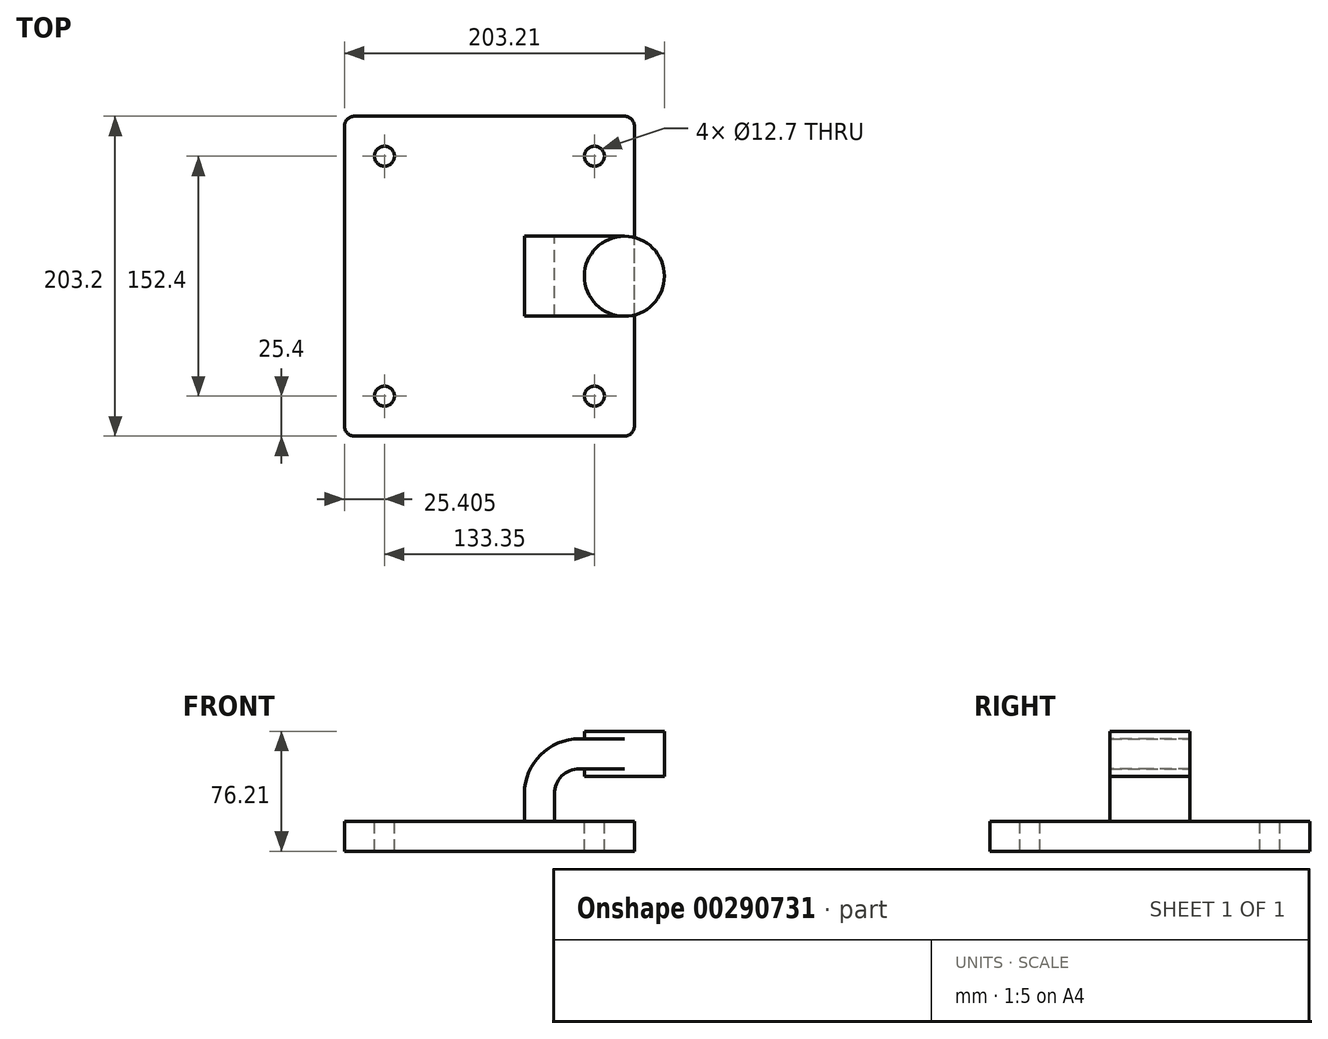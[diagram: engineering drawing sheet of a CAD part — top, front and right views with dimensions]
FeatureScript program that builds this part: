
annotation { "Feature Type Name" : "Feature", "Feature Type Description" : "" }
export const myFeature = defineFeature(function(context is Context, id is Id, definition is map)
    precondition{}
    {
        {
            var Q0;
            Q0=qCreatedBy(makeId("Front.planeOp"),FACE);
            var sketch = newSketch(context, id + "F0", { "sketchPlane" : qUnion([Q0])});
            skLineSegment(sketch, "E0.bottom", {"start": v(-41.28, -9.52) * mm, "end": v(41.28, -9.52) * mm});
            skLineSegment(sketch, "E0.top", {"start": v(-41.28, 9.53) * mm, "end": v(41.27, 9.53) * mm});
            skPoint(sketch, "E0.middle", {"position": v(0, 0) * mm});
            skLineSegment(sketch, "E1.bottom", {"start": v(60.32, 38.1) * mm, "end": v(111.12, 38.1) * mm});
            skLineSegment(sketch, "E1.top", {"start": v(60.32, 66.68) * mm, "end": v(111.12, 66.68) * mm});
            skLineSegment(sketch, "E1.left", {"start": v(60.32, 38.1) * mm, "end": v(60.32, 66.68) * mm});
            skLineSegment(sketch, "E1.right", {"start": v(111.12, 38.1) * mm, "end": v(111.12, 66.68) * mm});
            skPoint(sketch, "E1.middle", {"position": v(85.72, 52.39) * mm});
            skLineSegment(sketch, "E2", {"start": v(41.27, 9.52) * mm, "end": v(41.27, 27) * mm});
            skArc(sketch, "E3", {"start": v(41.27, 27) * mm, "mid": v(45.92, 38.23) * mm, "end": v(57.15, 42.88) * mm});
            skLineSegment(sketch, "E4", {"start": v(57.15, 42.88) * mm, "end": v(85.72, 42.88) * mm});
            skLineSegment(sketch, "E5.0", {"start": v(57.15, 61.93) * mm, "end": v(85.72, 61.93) * mm});
            skArc(sketch, "E5.1", {"start": v(22.22, 27) * mm, "mid": v(32.45, 51.7) * mm, "end": v(57.15, 61.93) * mm});
            skLineSegment(sketch, "E5.2", {"start": v(22.22, 9.52) * mm, "end": v(22.22, 27) * mm});
            skFitSpline(sketch, "E6", {"points": [v(-41.28, 9.52) * mm, v(57.15, 61.93) * mm], "startDerivative": vector(0.35, 59.87) * mm, "endDerivative": vector(73.58, -1.05) * mm});
            skLineSegment(sketch, "E7", {"start": v(85.72, 38.1) * mm, "end": v(85.72, 66.68) * mm});
            skLineSegment(sketch, "E8", {"start": v(-41.28, 9.53) * mm, "end": v(-92.08, 9.53) * mm});
            skLineSegment(sketch, "E9", {"start": v(-92.08, 9.52) * mm, "end": v(-92.08, -9.53) * mm});
            skLineSegment(sketch, "E10", {"start": v(-92.08, -9.52) * mm, "end": v(-41.27, -9.52) * mm});
            skLineSegment(sketch, "E11", {"start": v(41.27, 9.53) * mm, "end": v(92.08, 9.53) * mm});
            skLineSegment(sketch, "E12", {"start": v(92.08, 9.52) * mm, "end": v(92.08, -9.52) * mm});
            skLineSegment(sketch, "E13", {"start": v(92.08, -9.52) * mm, "end": v(41.28, -9.52) * mm});
            skSolve(sketch);
        }
        {
            var Q0;
            Q0=makeQuery(id+"F0.imprint","IMPRINT",FACE,{"disambiguationData":[TD([[makeQuery(id+"F0.imprint","IMPRINT",EDGE,{"derivedFrom":sQuery(id+"F0.wireOp",EDGE,"E0.bottom")}),1.0]])]});
            extrude(context, id + "F1", {"entities" : qUnion([Q0]), "endBound" : BoundingType.SYMMETRIC, "depth" : 203.2 * mm, "offsetDistance" : 25.4 * mm});
        }
        {
            var Q0;
            {var subQ1=sQuery(id+"F0.wireOp",EDGE,"E2");Q0=makeQuery(id+"F0.imprint","IMPRINT",FACE,{"disambiguationData":[TD([[makeQuery(id+"F0.imprint","IMPRINT",EDGE,{"derivedFrom":subQ1}),1.0]])]});}
            var Q1;
            {var subQ0=sQuery(id+"F0.wireOp",EDGE,"E4");var subQ1=sQuery(id+"F0.wireOp",EDGE,"E1.left");var subQ2=makeQuery(id+"F0.imprint","INTERSECT",VERTEX,{"derivedFrom":[subQ1,subQ0]});Q1=makeQuery(id+"F0.imprint","IMPRINT",FACE,{"disambiguationData":[TD([[makeQuery(id+"F0.imprint","IMPRINT",EDGE,{"disambiguationData":[TD([[subQ2,-1.0]])],"derivedFrom":subQ1}),-1.0]])]});}
            extrude(context, id + "F2", {"entities" : qUnion([Q0, Q1]), "operationType" : NewBodyOperationType.ADD, "endBound" : BoundingType.SYMMETRIC, "depth" : 50.8 * mm});
        }
        {
            var Q0;
            Q0=makeQuery(id+"F0.imprint","IMPRINT",FACE,{"disambiguationData":[TD([[makeQuery(id+"F0.imprint","IMPRINT",EDGE,{"derivedFrom":sQuery(id+"F0.wireOp",EDGE,"E5.1")}),1.0]])]});
            extrude(context, id + "F3", {"entities" : qUnion([Q0]), "operationType" : NewBodyOperationType.ADD, "endBound" : BoundingType.SYMMETRIC, "depth" : 15.88 * mm});
        }
        {
            var Q0;
            {var subQ4=sQuery(id+"F0.wireOp",EDGE,"E1.right");Q0=makeQuery(id+"F0.imprint","IMPRINT",FACE,{"disambiguationData":[TD([[makeQuery(id+"F0.imprint","IMPRINT",EDGE,{"derivedFrom":subQ4}),1.0]])]});}
            var Q1;
            Q1=sQuery(id+"F0.wireOp",EDGE,"E7");
            revolve(context, id + "F4", {"operationType" : NewBodyOperationType.ADD, "entities" : qUnion([Q0]), "axis" : qUnion([Q1]), "revolveType" : RevolveType.FULL});
        }
        {
            var Q0;
            Q0=makeQuery(id+"F1.opExtrude","CAP_EDGE",EDGE,{"disambiguationData":[OSD([sQuery(id+"F0.wireOp",EDGE,"E0.right")])],"isStart":false});
            var Q1;
            Q1=makeQuery(id+"F1.opExtrude","CAP_EDGE",EDGE,{"disambiguationData":[OSD([sQuery(id+"F0.wireOp",EDGE,"E0.right")])],"isStart":true});
            var Q2;
            Q2=makeQuery(id+"F1.opExtrude","CAP_EDGE",EDGE,{"disambiguationData":[OSD([sQuery(id+"F0.wireOp",EDGE,"E0.left")])],"isStart":false});
            var Q3;
            Q3=makeQuery(id+"F1.opExtrude","CAP_EDGE",EDGE,{"disambiguationData":[OSD([sQuery(id+"F0.wireOp",EDGE,"E0.left")])],"isStart":true});
            var Q4;
            Q4=makeQuery(id+"F1.opExtrude","CAP_EDGE",EDGE,{"disambiguationData":[OSD([sQuery(id+"F0.wireOp",EDGE,"E9")])],"isStart":false});
            var Q5;
            Q5=makeQuery(id+"F1.opExtrude","CAP_EDGE",EDGE,{"disambiguationData":[OSD([sQuery(id+"F0.wireOp",EDGE,"E12")])],"isStart":false});
            var Q6;
            Q6=makeQuery(id+"F1.opExtrude","CAP_EDGE",EDGE,{"disambiguationData":[OSD([sQuery(id+"F0.wireOp",EDGE,"E12")])],"isStart":true});
            var Q7;
            Q7=makeQuery(id+"F1.opExtrude","CAP_EDGE",EDGE,{"disambiguationData":[OSD([sQuery(id+"F0.wireOp",EDGE,"E9")])],"isStart":true});
            fillet(context, id + "F5", {"entities" : qUnion([Q0, Q1, Q2, Q3, Q4, Q5, Q6, Q7]), "radius" : 6.35 * mm, "tangentPropagation" : true, "allowEdgeOverflow" : false});
        }
        {
            var Q0;
            Q0=makeQuery(id+"F1.opExtrude","SWEPT_FACE",FACE,{"disambiguationData":[OSD([sQuery(id+"F0.wireOp",EDGE,"E0.top"),sQuery(id+"F0.wireOp",EDGE,"E8"),sQuery(id+"F0.wireOp",EDGE,"E11")])]});
            var sketch = newSketch(context, id + "F6", { "sketchPlane" : qUnion([Q0])});
            skCircle(sketch, "E14", {"center": v(66.67, 76.2) * mm, "radius": 6.35 * mm});
            skCircle(sketch, "E15.MirrorC", {"center": v(66.67, -76.2) * mm, "radius": 6.35 * mm});
            skCircle(sketch, "E16.MirrorC", {"center": v(-66.67, 76.2) * mm, "radius": 6.35 * mm});
            skCircle(sketch, "E17.MirrorC", {"center": v(-66.67, -76.2) * mm, "radius": 6.35 * mm});
            skSolve(sketch);
        }
        {
            var Q0;
            Q0 = qSketchRegion(id + "F6", true);
            extrude(context, id + "F7", {"entities" : qUnion([Q0]), "operationType" : NewBodyOperationType.REMOVE, "endBound" : BoundingType.THROUGH_ALL, "oppositeDirection" : true, "depth" : 25.4 * mm, "offsetDistance" : 25.4 * mm});
        }
    });
